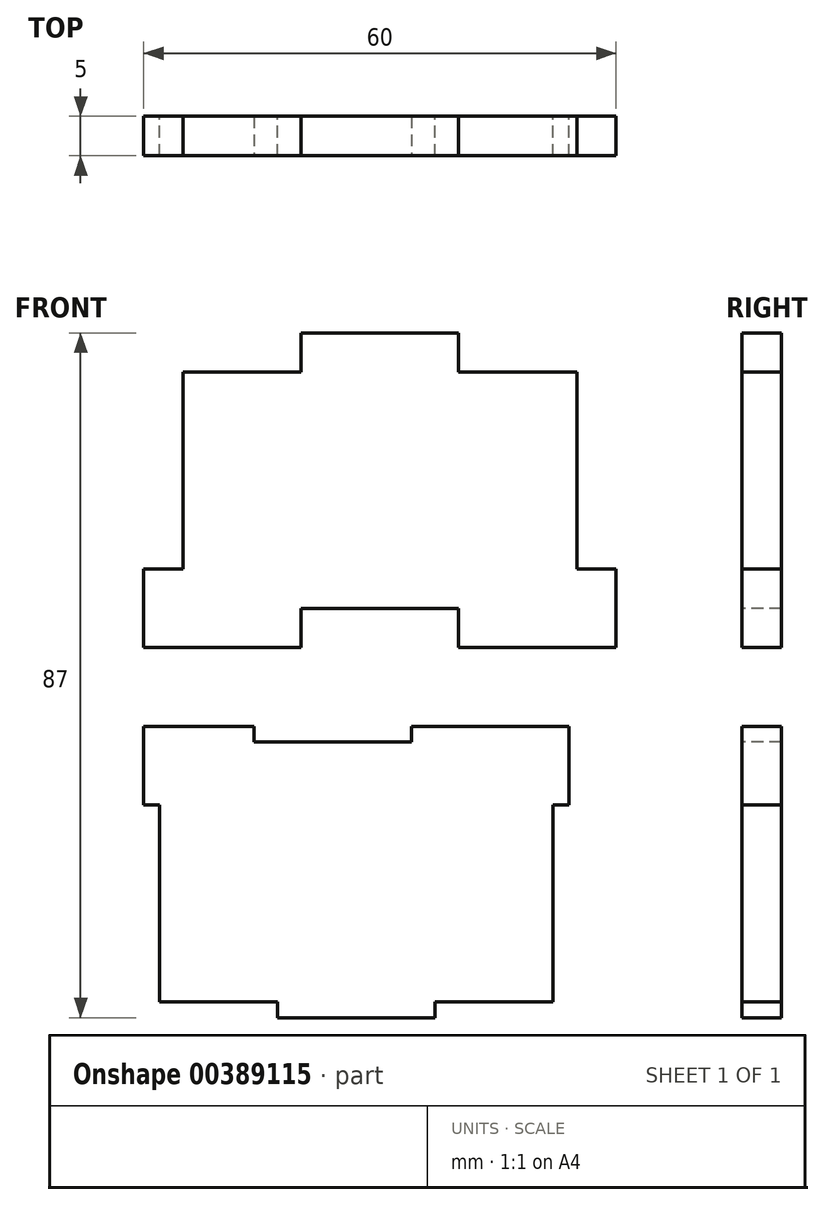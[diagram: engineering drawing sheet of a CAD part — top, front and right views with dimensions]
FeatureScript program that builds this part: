
annotation { "Feature Type Name" : "Feature", "Feature Type Description" : "" }
export const myFeature = defineFeature(function(context is Context, id is Id, definition is map)
    precondition{}
    {
        {
            var Q0;
            Q0=qCreatedBy(makeId("Front.planeOp"),FACE);
            var sketch = newSketch(context, id + "F0", { "sketchPlane" : qUnion([Q0])});
            skLineSegment(sketch, "E0", {"start": v(0, 0) * mm, "end": v(54, 0) * mm});
            skLineSegment(sketch, "E1", {"start": v(54, 0) * mm, "end": v(54, -10) * mm});
            skLineSegment(sketch, "E2", {"start": v(54, -10) * mm, "end": v(52, -10) * mm});
            skLineSegment(sketch, "E3", {"start": v(52, -10) * mm, "end": v(52, -35) * mm});
            skLineSegment(sketch, "E4", {"start": v(52, -35) * mm, "end": v(37, -35) * mm});
            skLineSegment(sketch, "E5", {"start": v(37, -35) * mm, "end": v(37, -37) * mm});
            skLineSegment(sketch, "E6", {"start": v(37, -37) * mm, "end": v(17, -37) * mm});
            skLineSegment(sketch, "E7", {"start": v(17, -37) * mm, "end": v(17, -35) * mm});
            skLineSegment(sketch, "E8", {"start": v(17, -35) * mm, "end": v(2, -35) * mm});
            skLineSegment(sketch, "E9", {"start": v(2, -35) * mm, "end": v(2, -10) * mm});
            skLineSegment(sketch, "E10", {"start": v(2, -10) * mm, "end": v(0, -10) * mm});
            skLineSegment(sketch, "E11", {"start": v(0, -10) * mm, "end": v(0, 0) * mm});
            skSolve(sketch);
        }
        {
            var Q0;
            Q0=qCreatedBy(makeId("Front.planeOp"),FACE);
            var sketch = newSketch(context, id + "F1", { "sketchPlane" : qUnion([Q0])});
            skLineSegment(sketch, "E12", {"start": v(0, 10) * mm, "end": v(60, 10) * mm});
            skLineSegment(sketch, "E13", {"start": v(60, 10) * mm, "end": v(60, 20) * mm});
            skLineSegment(sketch, "E14", {"start": v(60, 20) * mm, "end": v(55, 20) * mm});
            skLineSegment(sketch, "E15", {"start": v(55, 20) * mm, "end": v(55, 45) * mm});
            skLineSegment(sketch, "E16", {"start": v(55, 45) * mm, "end": v(40, 45) * mm});
            skLineSegment(sketch, "E17", {"start": v(40, 45) * mm, "end": v(40, 50) * mm});
            skLineSegment(sketch, "E18", {"start": v(40, 50) * mm, "end": v(20, 50) * mm});
            skLineSegment(sketch, "E19", {"start": v(20, 50) * mm, "end": v(20, 45) * mm});
            skLineSegment(sketch, "E20", {"start": v(20, 45) * mm, "end": v(5, 45) * mm});
            skLineSegment(sketch, "E21", {"start": v(5, 45) * mm, "end": v(5, 20) * mm});
            skLineSegment(sketch, "E22", {"start": v(5, 20) * mm, "end": v(0, 20) * mm});
            skLineSegment(sketch, "E23", {"start": v(0, 20) * mm, "end": v(0, 10) * mm});
            skSolve(sketch);
        }
        {
            var Q0;
            Q0=makeQuery(id+"F1.imprint","IMPRINT",FACE,{"disambiguationData":[TD([[makeQuery(id+"F1.imprint","IMPRINT",EDGE,{"derivedFrom":sQuery(id+"F1.wireOp",EDGE,"E12")}),1.0]])]});
            var Q1;
            Q1=makeQuery(id+"F0.imprint","IMPRINT",FACE,{"disambiguationData":[TD([[makeQuery(id+"F0.imprint","IMPRINT",EDGE,{"derivedFrom":sQuery(id+"F0.wireOp",EDGE,"E0")}),-1.0]])]});
            extrude(context, id + "F2", {"entities" : qUnion([Q0, Q1]), "depth" : 5 * mm});
        }
        {
            var Q0;
            Q0=makeQuery(id+"F2.opExtrude","CAP_FACE",FACE,{"disambiguationData":[OSD([sQuery(id+"F0.wireOp",EDGE,"E0"),sQuery(id+"F0.wireOp",EDGE,"E1"),sQuery(id+"F0.wireOp",EDGE,"E2"),sQuery(id+"F0.wireOp",EDGE,"E3"),sQuery(id+"F0.wireOp",EDGE,"E4"),sQuery(id+"F0.wireOp",EDGE,"E5"),sQuery(id+"F0.wireOp",EDGE,"E6"),sQuery(id+"F0.wireOp",EDGE,"E7"),sQuery(id+"F0.wireOp",EDGE,"E8"),sQuery(id+"F0.wireOp",EDGE,"E9"),sQuery(id+"F0.wireOp",EDGE,"E10"),sQuery(id+"F0.wireOp",EDGE,"E11")])],"isStart":false});
            var sketch = newSketch(context, id + "F3", { "sketchPlane" : qUnion([Q0])});
            skLineSegment(sketch, "E24.bottom", {"start": v(14, 8) * mm, "end": v(34, 8) * mm});
            skLineSegment(sketch, "E24.top", {"start": v(14, -2) * mm, "end": v(34, -2) * mm});
            skLineSegment(sketch, "E24.left", {"start": v(14, 8) * mm, "end": v(14, -2) * mm});
            skLineSegment(sketch, "E24.right", {"start": v(34, 8) * mm, "end": v(34, -2) * mm});
            skSolve(sketch);
        }
        {
            var Q0;
            Q0=makeQuery(id+"F2.opExtrude","CAP_FACE",FACE,{"disambiguationData":[OSD([sQuery(id+"F1.wireOp",EDGE,"E12"),sQuery(id+"F1.wireOp",EDGE,"E13"),sQuery(id+"F1.wireOp",EDGE,"E14"),sQuery(id+"F1.wireOp",EDGE,"E15"),sQuery(id+"F1.wireOp",EDGE,"E16"),sQuery(id+"F1.wireOp",EDGE,"E17"),sQuery(id+"F1.wireOp",EDGE,"E18"),sQuery(id+"F1.wireOp",EDGE,"E19"),sQuery(id+"F1.wireOp",EDGE,"E20"),sQuery(id+"F1.wireOp",EDGE,"E21"),sQuery(id+"F1.wireOp",EDGE,"E22"),sQuery(id+"F1.wireOp",EDGE,"E23")])],"isStart":false});
            var sketch = newSketch(context, id + "F4", { "sketchPlane" : qUnion([Q0])});
            skLineSegment(sketch, "E25.bottom", {"start": v(20, 15) * mm, "end": v(40, 15) * mm});
            skLineSegment(sketch, "E25.top", {"start": v(20, 5) * mm, "end": v(40, 5) * mm});
            skLineSegment(sketch, "E25.left", {"start": v(20, 15) * mm, "end": v(20, 5) * mm});
            skLineSegment(sketch, "E25.right", {"start": v(40, 15) * mm, "end": v(40, 5) * mm});
            skSolve(sketch);
        }
        {
            var Q0;
            {var subQ0=sQuery(id+"F3.wireOp",EDGE,"E24.top");Q0=makeQuery(id+"F3.imprint","IMPRINT",FACE,{"disambiguationData":[TD([[makeQuery(id+"F3.imprint","IMPRINT",EDGE,{"derivedFrom":subQ0}),1.0]])]});}
            extrude(context, id + "F5", {"entities" : qUnion([Q0]), "operationType" : NewBodyOperationType.REMOVE, "oppositeDirection" : true, "depth" : 5 * mm});
        }
        {
            var Q0;
            {var subQ0=sQuery(id+"F4.wireOp",EDGE,"E25.bottom");Q0=makeQuery(id+"F4.imprint","IMPRINT",FACE,{"disambiguationData":[TD([[makeQuery(id+"F4.imprint","IMPRINT",EDGE,{"derivedFrom":subQ0}),-1.0]])]});}
            extrude(context, id + "F6", {"entities" : qUnion([Q0]), "operationType" : NewBodyOperationType.REMOVE, "oppositeDirection" : true, "depth" : 5 * mm});
        }
    });
